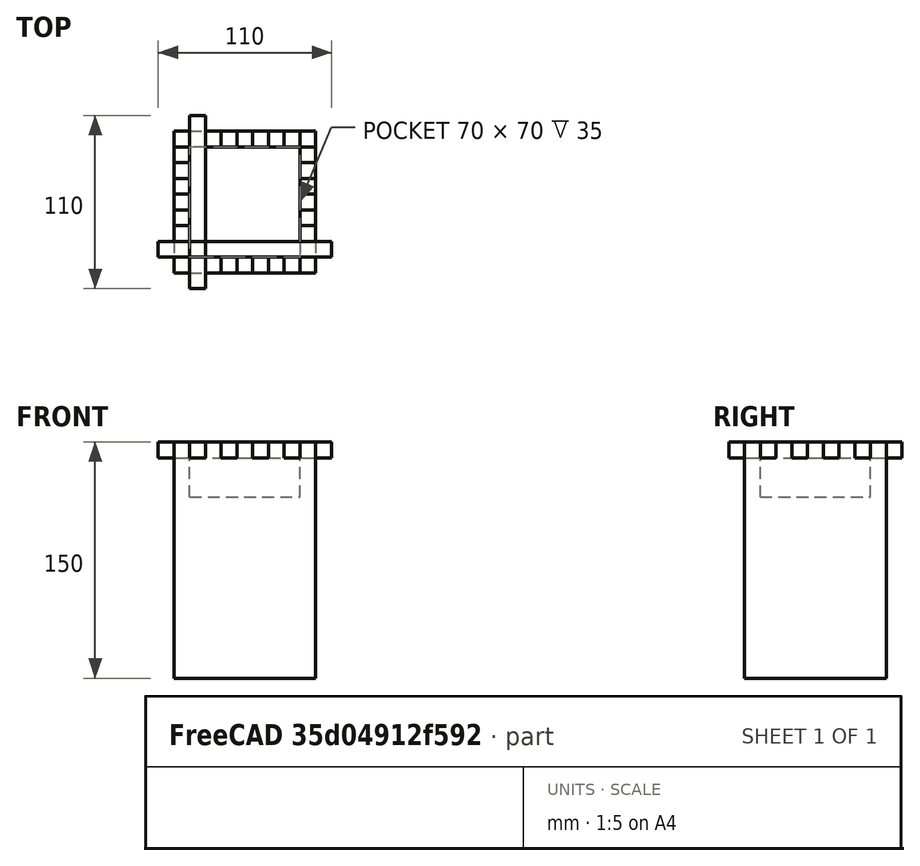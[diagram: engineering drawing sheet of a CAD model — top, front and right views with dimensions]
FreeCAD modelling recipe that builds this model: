
FCSTD DOCUMENT  (FreeCAD 0.21R33771 (Git))
Label: OJT1_T10R02_torre.20240120-193730
License: All rights reserved
LicenseURL: http://en.wikipedia.org/wiki/All_rights_reserved
objects: Part::Box×4, Part::Cut×3, Part::FeaturePython×2
note: 7 computed .brp shape members not serialized (recipe doc carries the construction recipe); baked Part::Feature solids carry a one-line shape summary decoded from their .brp

FEATURE [Part::Box] Box  label="Cube"
  AttacherType = Attacher::AttachEngine3D
  Height = 150
  Length = 90
  Width = 90
FEATURE [Part::Box] Box001  label="Cube001"
  AttacherType = Attacher::AttachEngine3D
  Height = 70
  Length = 70
  Placement = pos=(10,10,115) rot=(0,0,1;0rad)
  Width = 70
FEATURE [Part::Box] Box002  label="Cube002"
  AttacherType = Attacher::AttachEngine3D
  Height = 10
  Length = 110
  Placement = pos=(-10,10,140) rot=(0,0,1;0rad)
  Width = 10
FEATURE [Part::FeaturePython] Array  # Draft array (typed FeaturePython)
  AlwaysSyncPlacement = false
  Angle = 360
  ArrayType = 0
  Axis = (0,0,1)
  Base = -> Box002
  Center = (0,0,0)
  Count = 4
  ExpandArray = false
  Fuse = false
  IntervalAxis = (0,0,0)
  IntervalX = (0,20,0)
  IntervalY = (0,20,0)
  IntervalZ = (0,0,0)
  NumberCircles = 3
  NumberPolar = 5
  NumberX = 4
  NumberY = 1
  NumberZ = 1
  PlacementList = 4 placements: arithmetic series from (-10,10,140) step (0,20,0) to (-10,70,140)
  RadialDistance = 50
  ScaleList = (4) [(1,1,1),(1,1,1),(1,1,1),(1,1,1)]
  Symmetry = 1
  TangentialDistance = 25
FEATURE [Part::Box] Box003  label="Cube003"
  AttacherType = Attacher::AttachEngine3D
  Height = 10
  Length = 10
  Placement = pos=(10,-10,140) rot=(0,0,1;0rad)
  Width = 110
FEATURE [Part::FeaturePython] Array001  # Draft array (typed FeaturePython)
  AlwaysSyncPlacement = false
  Angle = 360
  ArrayType = 0
  Axis = (0,0,1)
  Base = -> Box003
  Center = (0,0,0)
  Count = 4
  ExpandArray = false
  Fuse = false
  IntervalAxis = (0,0,0)
  IntervalX = (20,0,0)
  IntervalY = (0,0,0)
  IntervalZ = (0,0,0)
  NumberCircles = 3
  NumberPolar = 5
  NumberX = 4
  NumberY = 1
  NumberZ = 1
  PlacementList = 4 placements: arithmetic series from (10,-10,140) step (20,0,0) to (70,-10,140)
  RadialDistance = 50
  ScaleList = (4) [(1,1,1),(1,1,1),(1,1,1),(1,1,1)]
  Symmetry = 1
  TangentialDistance = 25
FEATURE [Part::Cut] Cut
  Base = -> Box
  Refine = true
  Tool = -> Box001
FEATURE [Part::Cut] Cut001
  Base = -> Cut
  Refine = true
  Tool = -> Array
FEATURE [Part::Cut] Cut002  label="torre"
  Base = -> Cut001
  Refine = true
  Tool = -> Array001
